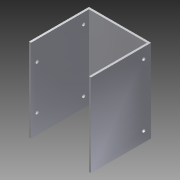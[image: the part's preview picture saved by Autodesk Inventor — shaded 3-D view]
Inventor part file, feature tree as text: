
AUTODESK INVENTOR PART (.ipt)
format: ipt  version: 2015 (Build 190159000, 159)  size: 130,560 bytes
history: native  units: mm
features: sketch x4, extrude x2, hole x2, other x1
ambient origin geometry x8: Origin, YZ Plane, XZ Plane, XY Plane, X Axis, Y Axis, Z Axis, Center Point
bodies: Body1 (feature_tree)
feature tree (9):
  other  "ソリッド1"
  extrude  "押し出し1"  Depth=60.0mm
  extrude  "押し出し2"  Depth=60.0mm
  hole  "穴1"  [1 undecoded]
  hole  "穴2"  [1 undecoded]
  sketch  "スケッチ1"
  sketch  "スケッチ2"
  sketch  "スケッチ3"
  sketch  "スケッチ4"
note: 2 required parameter values undecoded (feature->parameter linkage not recoverable at this tier; creation-order binding heuristic only, values carry confidence <= 0.55)
